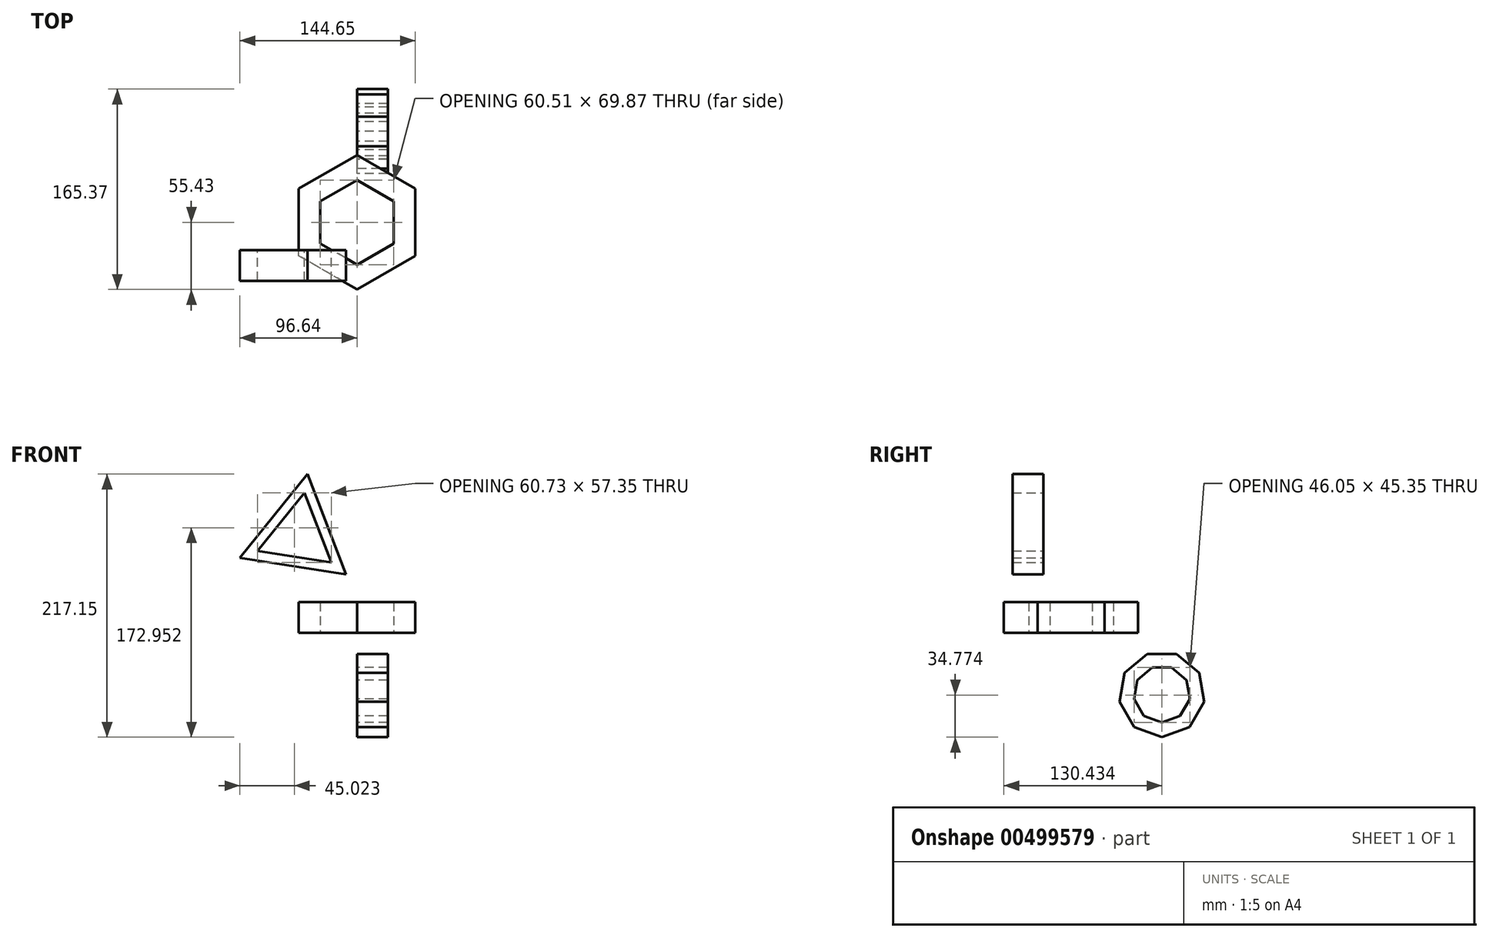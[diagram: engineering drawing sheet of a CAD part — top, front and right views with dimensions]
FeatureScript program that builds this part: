
annotation { "Feature Type Name" : "Feature", "Feature Type Description" : "" }
export const myFeature = defineFeature(function(context is Context, id is Id, definition is map)
    precondition{}
    {
        {
            var Q0;
            Q0=qCreatedBy(makeId("Top.planeOp"),FACE);
            var sketch = newSketch(context, id + "F0", { "sketchPlane" : qUnion([Q0])});
            skCircle(sketch, "E0.cCircle", {"center": v(0, 0) * mm, "radius": 48 * mm, "construction": true});
            skLineSegment(sketch, "E0.0", {"start": v(-48, -27.72) * mm, "end": v(-48, 27.72) * mm});
            skLineSegment(sketch, "E0.1", {"start": v(-48, 27.72) * mm, "end": v(0, 55.43) * mm});
            skLineSegment(sketch, "E0.2", {"start": v(0, 55.43) * mm, "end": v(48, 27.72) * mm});
            skLineSegment(sketch, "E0.3", {"start": v(48, 27.72) * mm, "end": v(48, -27.72) * mm});
            skLineSegment(sketch, "E0.4", {"start": v(48, -27.72) * mm, "end": v(0, -55.43) * mm});
            skLineSegment(sketch, "E0.5", {"start": v(0, -55.43) * mm, "end": v(-48, -27.72) * mm});
            skPoint(sketch, "E0.0.midPoint", {"position": v(-48, 0) * mm});
            skCircle(sketch, "E1.cCircle", {"center": v(0, 0) * mm, "radius": 30.25 * mm, "construction": true});
            skLineSegment(sketch, "E1.0", {"start": v(-30.25, -17.47) * mm, "end": v(-30.25, 17.47) * mm});
            skLineSegment(sketch, "E1.1", {"start": v(-30.25, 17.47) * mm, "end": v(0, 34.94) * mm});
            skLineSegment(sketch, "E1.2", {"start": v(0, 34.94) * mm, "end": v(30.25, 17.47) * mm});
            skLineSegment(sketch, "E1.3", {"start": v(30.25, 17.47) * mm, "end": v(30.25, -17.47) * mm});
            skLineSegment(sketch, "E1.4", {"start": v(30.25, -17.47) * mm, "end": v(0, -34.94) * mm});
            skLineSegment(sketch, "E1.5", {"start": v(0, -34.94) * mm, "end": v(-30.25, -17.47) * mm});
            skPoint(sketch, "E1.0.midPoint", {"position": v(-30.25, 0) * mm});
            skSolve(sketch);
        }
        {
            var Q0;
            Q0=qSketchRegion(id+"F0",true);
            extrude(context, id + "F1", {"entities" : qUnion([Q0]), "depth" : 25.4 * mm});
        }
        {
            var Q0;
            Q0=qCreatedBy(makeId("Front.planeOp"),FACE);
            var sketch = newSketch(context, id + "F2", { "sketchPlane" : qUnion([Q0])});
            skCircle(sketch, "E2.cCircle", {"center": v(-69.7, -28.7) * mm, "radius": 25.6 * mm, "construction": true});
            skLineSegment(sketch, "E2.0", {"start": v(-29.86, -60.85) * mm, "end": v(-117.46, -47.11) * mm});
            skLineSegment(sketch, "E2.1", {"start": v(-117.46, -47.11) * mm, "end": v(-61.76, 21.89) * mm});
            skLineSegment(sketch, "E2.2", {"start": v(-61.76, 21.89) * mm, "end": v(-29.86, -60.85) * mm});
            skPoint(sketch, "E2.0.midPoint", {"position": v(-73.66, -53.98) * mm});
            skCircle(sketch, "E3.cCircle", {"center": v(-69.7, -28.7) * mm, "radius": 17.74 * mm, "construction": true});
            skLineSegment(sketch, "E3.0", {"start": v(-102.8, -41.46) * mm, "end": v(-64.2, 6.37) * mm});
            skLineSegment(sketch, "E3.1", {"start": v(-64.2, 6.37) * mm, "end": v(-42.08, -50.99) * mm});
            skLineSegment(sketch, "E3.2", {"start": v(-42.08, -50.99) * mm, "end": v(-102.8, -41.46) * mm});
            skPoint(sketch, "E3.0.midPoint", {"position": v(-83.5, -17.54) * mm});
            skSolve(sketch);
        }
        {
            var Q0;
            Q0=qSketchRegion(id+"F2",true);
            extrude(context, id + "F3", {"entities" : qUnion([Q0]), "depth" : 25.4 * mm});
        }
        {
            var Q0;
            Q0=makeQuery(id+"F3.opExtrude","SWEPT_BODY",BODY,{"disambiguationData":[OSD([sQuery(id+"F2.wireOp",EDGE,"E2.0"),sQuery(id+"F2.wireOp",EDGE,"E2.1"),sQuery(id+"F2.wireOp",EDGE,"E2.2"),sQuery(id+"F2.wireOp",EDGE,"E3.0"),sQuery(id+"F2.wireOp",EDGE,"E3.1"),sQuery(id+"F2.wireOp",EDGE,"E3.2")])]});
            transform(context, id + "F4", {"entities" : qUnion([Q0]), "transformType" : TransformType.TRANSLATION_3D, "dx" : 42.16 * mm, "dy" : 18.8 * mm, "dz" : 40.4 * mm, "makeCopy" : false});
        }
        {
            var Q0;
            Q0=qCreatedBy(makeId("Right.planeOp"),FACE);
            var sketch = newSketch(context, id + "F5", { "sketchPlane" : qUnion([Q0])});
            skCircle(sketch, "E4.cCircle", {"center": v(75, -50.56) * mm, "radius": 21.97 * mm, "construction": true});
            skLineSegment(sketch, "E4.0", {"start": v(67, -28.6) * mm, "end": v(83, -28.6) * mm});
            skLineSegment(sketch, "E4.1", {"start": v(83, -28.6) * mm, "end": v(95.25, -38.87) * mm});
            skLineSegment(sketch, "E4.2", {"start": v(95.25, -38.87) * mm, "end": v(98.03, -54.62) * mm});
            skLineSegment(sketch, "E4.3", {"start": v(98.03, -54.62) * mm, "end": v(90.03, -68.47) * mm});
            skLineSegment(sketch, "E4.4", {"start": v(90.03, -68.47) * mm, "end": v(75, -73.94) * mm});
            skLineSegment(sketch, "E4.5", {"start": v(75, -73.94) * mm, "end": v(59.98, -68.47) * mm});
            skLineSegment(sketch, "E4.6", {"start": v(59.98, -68.47) * mm, "end": v(51.98, -54.62) * mm});
            skLineSegment(sketch, "E4.7", {"start": v(51.98, -54.62) * mm, "end": v(54.76, -38.87) * mm});
            skLineSegment(sketch, "E4.8", {"start": v(54.76, -38.87) * mm, "end": v(67, -28.6) * mm});
            skPoint(sketch, "E4.0.midPoint", {"position": v(75, -28.6) * mm});
            skCircle(sketch, "E5.cCircle", {"center": v(75, -50.56) * mm, "radius": 33.34 * mm, "construction": true});
            skLineSegment(sketch, "E5.0", {"start": v(62.87, -17.22) * mm, "end": v(87.14, -17.22) * mm});
            skLineSegment(sketch, "E5.1", {"start": v(87.14, -17.22) * mm, "end": v(105.73, -32.82) * mm});
            skLineSegment(sketch, "E5.2", {"start": v(105.73, -32.82) * mm, "end": v(109.94, -56.72) * mm});
            skLineSegment(sketch, "E5.3", {"start": v(109.94, -56.72) * mm, "end": v(97.81, -77.74) * mm});
            skLineSegment(sketch, "E5.4", {"start": v(97.81, -77.74) * mm, "end": v(75, -86.04) * mm});
            skLineSegment(sketch, "E5.5", {"start": v(75, -86.04) * mm, "end": v(52.2, -77.74) * mm});
            skLineSegment(sketch, "E5.6", {"start": v(52.2, -77.74) * mm, "end": v(40.06, -56.72) * mm});
            skLineSegment(sketch, "E5.7", {"start": v(40.06, -56.72) * mm, "end": v(44.28, -32.82) * mm});
            skLineSegment(sketch, "E5.8", {"start": v(44.28, -32.82) * mm, "end": v(62.87, -17.22) * mm});
            skPoint(sketch, "E5.0.midPoint", {"position": v(75, -17.22) * mm});
            skSolve(sketch);
        }
        {
            var Q0;
            Q0=qSketchRegion(id+"F5",true);
            extrude(context, id + "F6", {"entities" : qUnion([Q0]), "depth" : 25.4 * mm});
        }
        {
            var Q0;
            Q0=makeQuery(id+"F3.opExtrude","SWEPT_BODY",BODY,{"disambiguationData":[OSD([sQuery(id+"F2.wireOp",EDGE,"E2.0"),sQuery(id+"F2.wireOp",EDGE,"E2.1"),sQuery(id+"F2.wireOp",EDGE,"E2.2"),sQuery(id+"F2.wireOp",EDGE,"E3.0"),sQuery(id+"F2.wireOp",EDGE,"E3.1"),sQuery(id+"F2.wireOp",EDGE,"E3.2")])]});
            transform(context, id + "F7", {"entities" : qUnion([Q0]), "transformType" : TransformType.TRANSLATION_3D, "dx" : -21.34 * mm, "dy" : -41.66 * mm, "dz" : 68.83 * mm, "makeCopy" : false});
        }
    });
